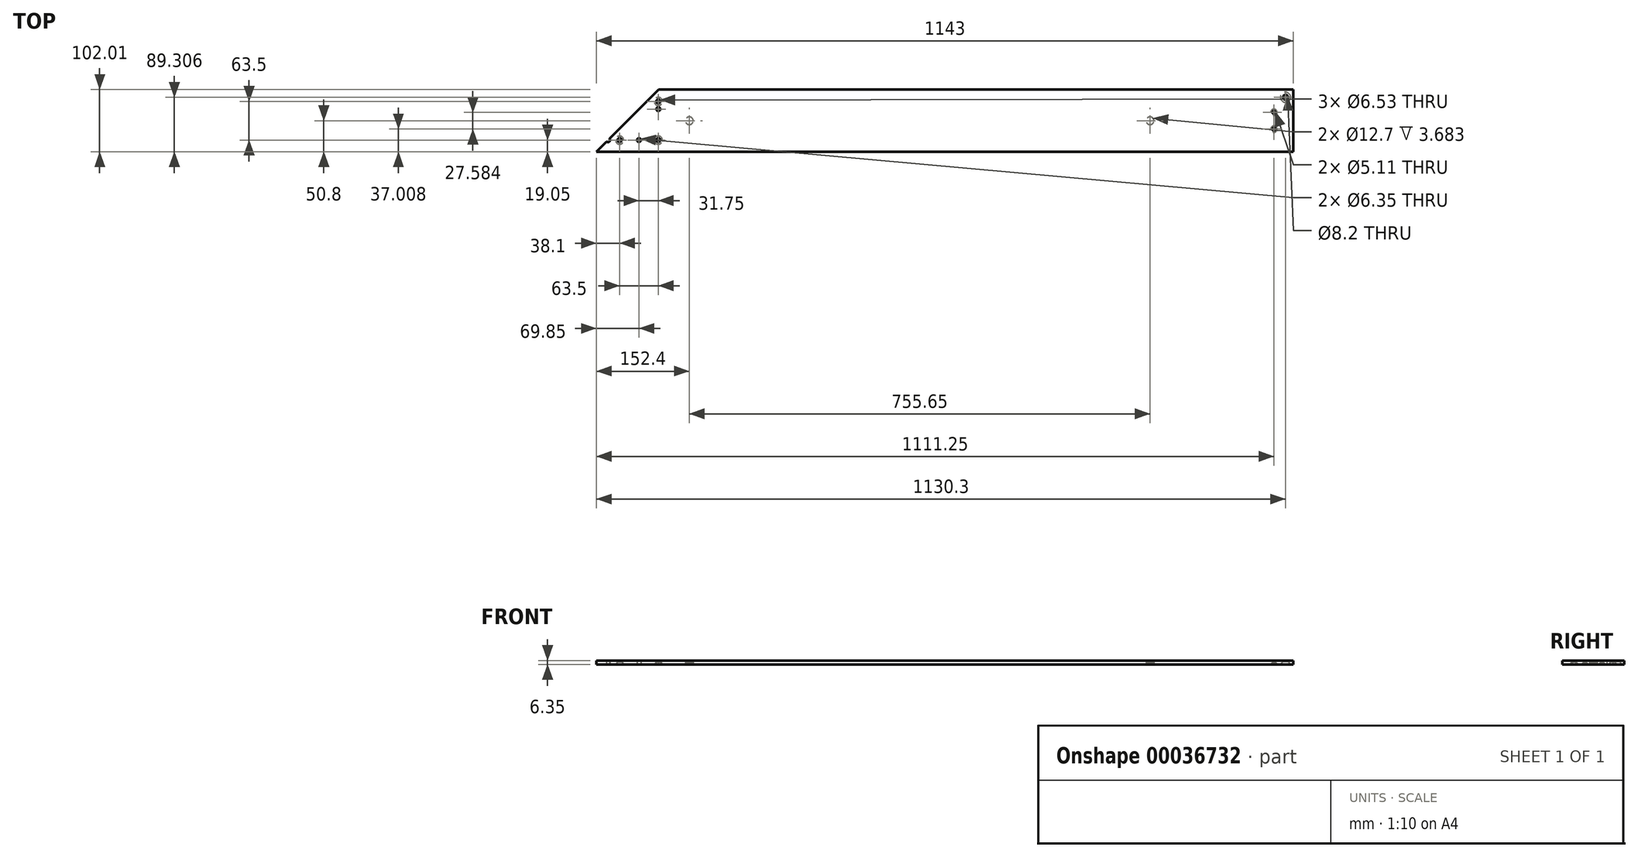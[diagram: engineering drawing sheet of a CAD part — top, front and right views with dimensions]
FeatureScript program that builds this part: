
annotation { "Feature Type Name" : "Feature", "Feature Type Description" : "" }
export const myFeature = defineFeature(function(context is Context, id is Id, definition is map)
    precondition{}
    {
        {
            var Q0;
            Q0=qCreatedBy(makeId("Top.planeOp"),FACE);
            var sketch = newSketch(context, id + "F0", { "sketchPlane" : qUnion([Q0])});
            skLineSegment(sketch, "E0", {"start": v(0, 0) * mm, "end": v(1041.4, 0) * mm});
            skLineSegment(sketch, "E1", {"start": v(0, 0) * mm, "end": v(-101.6, -101.6) * mm});
            skLineSegment(sketch, "E2", {"start": v(-101.6, -101.6) * mm, "end": v(1041.4, -101.6) * mm});
            skLineSegment(sketch, "E3", {"start": v(1041.4, 0) * mm, "end": v(1041.4, -101.6) * mm});
            skSolve(sketch);
        }
        {
            var Q0;
            Q0 = qSketchRegion(id + "F0", true);
            extrude(context, id + "F1", {"entities" : qUnion([Q0]), "depth" : 6.35 * mm});
        }
        {
            var Q0;
            Q0=makeQuery(id+"F1.opExtrude","CAP_FACE",FACE,{"disambiguationData":[OSD([sQuery(id+"F0.wireOp",EDGE,"E0"),sQuery(id+"F0.wireOp",EDGE,"E1"),sQuery(id+"F0.wireOp",EDGE,"E2"),sQuery(id+"F0.wireOp",EDGE,"E3")])],"isStart":true});
            var sketch = newSketch(context, id + "F2", { "sketchPlane" : qUnion([Q0])});
            skPoint(sketch, "E4", {"position": v(-63.5, 82.55) * mm});
            skPoint(sketch, "E5", {"position": v(0, 19.05) * mm});
            skPoint(sketch, "E6", {"position": v(0, 82.55) * mm});
            skSolve(sketch);
        }
        {
            var Q0;
            Q0=sQuery(id+"F2.wireOp",VERTEX,"E4");
            var Q1;
            Q1=sQuery(id+"F2.wireOp",VERTEX,"E6");
            var Q2;
            Q2=sQuery(id+"F2.wireOp",VERTEX,"E5");
            var Q3;
            Q3=makeQuery(id+"F1.opExtrude","SWEPT_BODY",BODY,{"disambiguationData":[OSD([sQuery(id+"F0.wireOp",EDGE,"E0"),sQuery(id+"F0.wireOp",EDGE,"E1"),sQuery(id+"F0.wireOp",EDGE,"E2"),sQuery(id+"F0.wireOp",EDGE,"E3")])]});
            hole(context, id + "F3", {"style" : HoleStyle.C_SINK, "endStyle" : HoleEndStyle.THROUGH, "standardTappedOrClearance" : lookupTablePath({ "standard" : "ANSI", "fit" : "Close", "size" : "1/4", "type" : "Clearance" }), "standardBlindInLast" : lookupTablePath({ "fit" : "Close", "standard" : "ANSI", "size" : "1/4", "type" : "Clearance" }), "holeDiameter" : 6.53 * mm, "cSinkDiameter" : 13.5 * mm, "cSinkAngle" : 82 * degree, "tappedDepth" : 12.7 * mm, "tapClearance" : 3, "locations" : qUnion([Q0, Q1, Q2]), "scope" : qUnion([Q3])});
        }
        {
            var Q0;
            Q0=makeQuery(id+"F1.opExtrude","CAP_FACE",FACE,{"disambiguationData":[OSD([sQuery(id+"F0.wireOp",EDGE,"E0"),sQuery(id+"F0.wireOp",EDGE,"E1"),sQuery(id+"F0.wireOp",EDGE,"E2"),sQuery(id+"F0.wireOp",EDGE,"E3")])],"isStart":true});
            var sketch = newSketch(context, id + "F4", { "sketchPlane" : qUnion([Q0])});
            skCircle(sketch, "E7", {"center": v(50.8, 50.8) * mm, "radius": 6.35 * mm});
            skCircle(sketch, "E8", {"center": v(806.45, 50.8) * mm, "radius": 6.35 * mm});
            skSolve(sketch);
        }
        {
            var Q0;
            Q0 = qSketchRegion(id + "F4", true);
            extrude(context, id + "F5", {"entities" : qUnion([Q0]), "operationType" : NewBodyOperationType.REMOVE, "oppositeDirection" : true, "depth" : 3.68 * mm, "offsetDistance" : 25.4 * mm});
        }
        {
            var Q0;
            Q0=makeQuery(id+"F1.opExtrude","CAP_FACE",FACE,{"disambiguationData":[OSD([sQuery(id+"F0.wireOp",EDGE,"E0"),sQuery(id+"F0.wireOp",EDGE,"E1"),sQuery(id+"F0.wireOp",EDGE,"E2"),sQuery(id+"F0.wireOp",EDGE,"E3")])],"isStart":true});
            var sketch = newSketch(context, id + "F6", { "sketchPlane" : qUnion([Q0])});
            skLineSegment(sketch, "E9", {"start": v(1041.4, 50.8) * mm, "end": v(885.8, 50.8) * mm, "construction": true});
            skPoint(sketch, "E9.endSnap0", {"position": v(1041.4, 50.8) * mm});
            skPoint(sketch, "E10", {"position": v(1009.65, 64.6) * mm});
            skPoint(sketch, "E11", {"position": v(1009.65, 37) * mm});
            skSolve(sketch);
        }
        {
            var Q0;
            Q0=sQuery(id+"F6.wireOp",VERTEX,"E10");
            var Q1;
            Q1=sQuery(id+"F6.wireOp",VERTEX,"E11");
            var Q2;
            Q2=makeQuery(id+"F1.opExtrude","SWEPT_BODY",BODY,{"disambiguationData":[OSD([sQuery(id+"F0.wireOp",EDGE,"E0"),sQuery(id+"F0.wireOp",EDGE,"E1"),sQuery(id+"F0.wireOp",EDGE,"E2"),sQuery(id+"F0.wireOp",EDGE,"E3")])]});
            hole(context, id + "F7", {"style" : HoleStyle.C_SINK, "endStyle" : HoleEndStyle.THROUGH, "standardTappedOrClearance" : lookupTablePath({ "standard" : "ANSI", "fit" : "Normal (ASME)", "size" : "#10", "type" : "Clearance" }), "standardBlindInLast" : lookupTablePath({ "fit" : "Free", "standard" : "ANSI", "size" : "#10", "type" : "Clearance" }), "holeDiameter" : 5.1 * mm, "cSinkDiameter" : 10.44 * mm, "cSinkAngle" : 82 * degree, "tappedDepth" : 6.35 * mm, "tapClearance" : 3, "locations" : qUnion([Q0, Q1]), "scope" : qUnion([Q2]), "majorDiameter" : 6.35 * mm});
        }
        {
            var Q0;
            Q0=makeQuery(id+"F1.opExtrude","CAP_FACE",FACE,{"disambiguationData":[OSD([sQuery(id+"F0.wireOp",EDGE,"E0"),sQuery(id+"F0.wireOp",EDGE,"E1"),sQuery(id+"F0.wireOp",EDGE,"E2"),sQuery(id+"F0.wireOp",EDGE,"E3")])],"isStart":true});
            var sketch = newSketch(context, id + "F8", { "sketchPlane" : qUnion([Q0])});
            skPoint(sketch, "E12", {"position": v(-82.55, 82.55) * mm});
            skSolve(sketch);
        }
        {
            var Q0;
            Q0=sQuery(id+"F8.wireOp",VERTEX,"E12");
            var Q1;
            Q1=makeQuery(id+"F1.opExtrude","SWEPT_BODY",BODY,{"disambiguationData":[OSD([sQuery(id+"F0.wireOp",EDGE,"E0"),sQuery(id+"F0.wireOp",EDGE,"E1"),sQuery(id+"F0.wireOp",EDGE,"E2"),sQuery(id+"F0.wireOp",EDGE,"E3")])]});
            hole(context, id + "F9", {"style" : HoleStyle.SIMPLE, "endStyle" : HoleEndStyle.THROUGH, "standardTappedOrClearance" : lookupTablePath({ "standard" : "ANSI", "fit" : "Normal (ASME)", "size" : "1/4", "type" : "Clearance" }), "standardBlindInLast" : lookupTablePath({ "fit" : "Free", "standard" : "ANSI", "size" : "1/4", "type" : "Clearance" }), "holeDiameter" : 6.76 * mm, "isTappedThrough" : true, "tappedDepth" : 6.35 * mm, "tapClearance" : 3, "locations" : qUnion([Q0]), "scope" : qUnion([Q1])});
        }
        {
            var Q0;
            Q0=makeQuery(id+"F1.opExtrude","CAP_FACE",FACE,{"disambiguationData":[OSD([sQuery(id+"F0.wireOp",EDGE,"E0"),sQuery(id+"F0.wireOp",EDGE,"E1"),sQuery(id+"F0.wireOp",EDGE,"E2"),sQuery(id+"F0.wireOp",EDGE,"E3")])],"isStart":true});
            var sketch = newSketch(context, id + "F10", { "sketchPlane" : qUnion([Q0])});
            skCircle(sketch, "E13", {"center": v(-31.75, 82.55) * mm, "radius": 3.18 * mm});
            skCircle(sketch, "E14", {"center": v(0, 31.75) * mm, "radius": 3.18 * mm});
            skLineSegment(sketch, "E15", {"start": v(-63.5, 82.55) * mm, "end": v(0, 82.55) * mm, "construction": true});
            skLineSegment(sketch, "E16", {"start": v(0, 82.55) * mm, "end": v(0, 19.05) * mm, "construction": true});
            skSolve(sketch);
        }
        {
            var Q0;
            Q0=makeQuery(id+"F10.imprint","IMPRINT",FACE,{"disambiguationData":[TD([[makeQuery(id+"F10.imprint","IMPRINT",EDGE,{"derivedFrom":sQuery(id+"F10.wireOp",EDGE,"E13")}),1.0]])]});
            var Q1;
            Q1=makeQuery(id+"F10.imprint","IMPRINT",FACE,{"disambiguationData":[TD([[makeQuery(id+"F10.imprint","IMPRINT",EDGE,{"derivedFrom":sQuery(id+"F10.wireOp",EDGE,"E14")}),1.0]])]});
            extrude(context, id + "F11", {"entities" : qUnion([Q0, Q1]), "operationType" : NewBodyOperationType.REMOVE, "endBound" : BoundingType.THROUGH_ALL, "oppositeDirection" : true, "depth" : 25.4 * mm});
        }
        {
            var Q0;
            Q0=qCreatedBy(makeId("Top.planeOp"),FACE);
            var sketch = newSketch(context, id + "F12", { "sketchPlane" : qUnion([Q0])});
            skLineSegment(sketch, "E17.bottom", {"start": v(0, 0) * mm, "end": v(1041.4, 0) * mm});
            skLineSegment(sketch, "E17.top", {"start": v(0, 0.4) * mm, "end": v(1041.4, 0.4) * mm});
            skLineSegment(sketch, "E17.left", {"start": v(0, 0) * mm, "end": v(0, 0.4) * mm});
            skLineSegment(sketch, "E17.right", {"start": v(1041.4, 0) * mm, "end": v(1041.4, 0.4) * mm});
            skSolve(sketch);
        }
        {
            var Q0;
            Q0=makeQuery(id+"F12.imprint","IMPRINT",FACE,{"disambiguationData":[TD([[makeQuery(id+"F12.imprint","IMPRINT",EDGE,{"derivedFrom":sQuery(id+"F12.wireOp",EDGE,"E17.bottom")}),1.0]])]});
            extrude(context, id + "F13", {"entities" : qUnion([Q0]), "operationType" : NewBodyOperationType.ADD, "depth" : 6.35 * mm, "offsetDistance" : 25.4 * mm});
        }
        {
            var Q0;
            Q0=makeQuery(id+"F13.boolean.opBoolean","MERGE",FACE,{"derivedFrom":[makeQuery(id+"F1.opExtrude","CAP_FACE",FACE,{"disambiguationData":[OSD([sQuery(id+"F0.wireOp",EDGE,"E0"),sQuery(id+"F0.wireOp",EDGE,"E1"),sQuery(id+"F0.wireOp",EDGE,"E2"),sQuery(id+"F0.wireOp",EDGE,"E3")])],"isStart":false}),makeQuery(id+"F13.opExtrude","CAP_FACE",FACE,{"disambiguationData":[OSD([sQuery(id+"F12.wireOp",EDGE,"E17.bottom"),sQuery(id+"F12.wireOp",EDGE,"E17.top"),sQuery(id+"F12.wireOp",EDGE,"E17.left"),sQuery(id+"F12.wireOp",EDGE,"E17.right")])],"isStart":false})]});
            var sketch = newSketch(context, id + "F14", { "sketchPlane" : qUnion([Q0])});
            skLineSegment(sketch, "E18", {"start": v(0, 0) * mm, "end": v(0, 0.4) * mm});
            skLineSegment(sketch, "E19", {"start": v(0, 0.4) * mm, "end": v(0.4, 0.4) * mm});
            skLineSegment(sketch, "E20", {"start": v(0.4, 0.4) * mm, "end": v(0, 0) * mm});
            skSolve(sketch);
        }
        {
            var Q0;
            Q0=makeQuery(id+"F14.imprint","IMPRINT",FACE,{"disambiguationData":[TD([[makeQuery(id+"F14.imprint","IMPRINT",EDGE,{"derivedFrom":sQuery(id+"F14.wireOp",EDGE,"E18")}),-1.0]])]});
            extrude(context, id + "F15", {"entities" : qUnion([Q0]), "operationType" : NewBodyOperationType.REMOVE, "oppositeDirection" : true, "depth" : 25.4 * mm, "offsetDistance" : 25.4 * mm});
        }
        {
            var Q0;
            Q0=makeQuery(id+"F13.boolean.opBoolean","MERGE",FACE,{"derivedFrom":[makeQuery(id+"F1.opExtrude","CAP_FACE",FACE,{"disambiguationData":[OSD([sQuery(id+"F0.wireOp",EDGE,"E0"),sQuery(id+"F0.wireOp",EDGE,"E1"),sQuery(id+"F0.wireOp",EDGE,"E2"),sQuery(id+"F0.wireOp",EDGE,"E3")])],"isStart":true}),makeQuery(id+"F13.opExtrude","CAP_FACE",FACE,{"disambiguationData":[OSD([sQuery(id+"F12.wireOp",EDGE,"E17.bottom"),sQuery(id+"F12.wireOp",EDGE,"E17.top"),sQuery(id+"F12.wireOp",EDGE,"E17.left"),sQuery(id+"F12.wireOp",EDGE,"E17.right")])],"isStart":true})]});
            var sketch = newSketch(context, id + "F16", { "sketchPlane" : qUnion([Q0])});
            skPoint(sketch, "E21", {"position": v(1028.7, 12.3) * mm});
            skSolve(sketch);
        }
        {
            var Q0;
            Q0=sQuery(id+"F16.wireOp",VERTEX,"E21");
            var Q1;
            Q1=makeQuery(id+"F1.opExtrude","SWEPT_BODY",BODY,{"disambiguationData":[OSD([sQuery(id+"F0.wireOp",EDGE,"E0"),sQuery(id+"F0.wireOp",EDGE,"E1"),sQuery(id+"F0.wireOp",EDGE,"E2"),sQuery(id+"F0.wireOp",EDGE,"E3")])]});
            hole(context, id + "F17", {"style" : HoleStyle.C_SINK, "endStyle" : HoleEndStyle.THROUGH, "standardTappedOrClearance" : lookupTablePath({ "standard" : "ANSI", "fit" : "Close", "size" : "5/16", "type" : "Clearance" }), "standardBlindInLast" : lookupTablePath({ "fit" : "Close", "standard" : "ANSI", "size" : "5/16", "type" : "Clearance" }), "holeDiameter" : 8.2 * mm, "cSinkDiameter" : 16.66 * mm, "cSinkAngle" : 82 * degree, "majorDiameter" : 6.35 * mm, "tappedDepth" : 6.35 * mm, "tapClearance" : 3, "locations" : qUnion([Q0]), "scope" : qUnion([Q1])});
        }
    });
